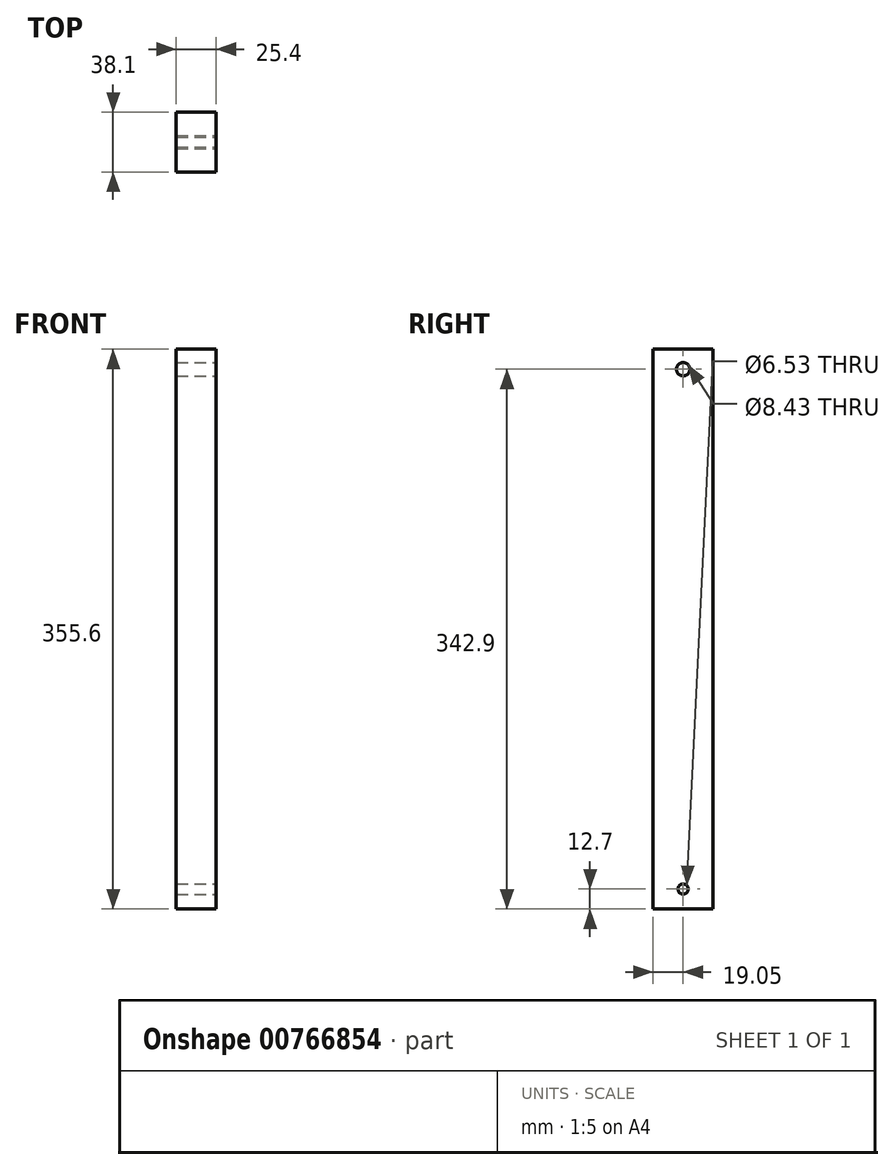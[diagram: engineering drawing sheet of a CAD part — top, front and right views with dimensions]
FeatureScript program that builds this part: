
annotation { "Feature Type Name" : "Feature", "Feature Type Description" : "" }
export const myFeature = defineFeature(function(context is Context, id is Id, definition is map)
    precondition{}
    {
        {
            var Q0;
            Q0=qCreatedBy(makeId("Right.planeOp"),FACE);
            var sketch = newSketch(context, id + "F0", { "sketchPlane" : qUnion([Q0])});
            skLineSegment(sketch, "E0.bottom", {"start": v(-19.05, 177.8) * mm, "end": v(19.05, 177.8) * mm});
            skLineSegment(sketch, "E0.top", {"start": v(-19.05, -177.8) * mm, "end": v(19.05, -177.8) * mm});
            skLineSegment(sketch, "E0.left", {"start": v(-19.05, 177.8) * mm, "end": v(-19.05, -177.8) * mm});
            skLineSegment(sketch, "E0.right", {"start": v(19.05, 177.8) * mm, "end": v(19.05, -177.8) * mm});
            skPoint(sketch, "E0.middle", {"position": v(0, 0) * mm});
            skSolve(sketch);
        }
        {
            var Q0;
            Q0=makeQuery(id+"F0.imprint","IMPRINT",FACE,{"disambiguationData":[TD([[makeQuery(id+"F0.imprint","IMPRINT",EDGE,{"derivedFrom":sQuery(id+"F0.wireOp",EDGE,"E0.bottom")}),-1.0]])]});
            extrude(context, id + "F1", {"entities" : qUnion([Q0]), "depth" : 25.4 * mm, "offsetDistance" : 25.4 * mm});
        }
        {
            var Q0;
            Q0=makeQuery(id+"F1.opExtrude","CAP_FACE",FACE,{"disambiguationData":[OSD([sQuery(id+"F0.wireOp",EDGE,"E0.bottom"),sQuery(id+"F0.wireOp",EDGE,"E0.top"),sQuery(id+"F0.wireOp",EDGE,"E0.left"),sQuery(id+"F0.wireOp",EDGE,"E0.right")])],"isStart":false});
            var sketch = newSketch(context, id + "F2", { "sketchPlane" : qUnion([Q0])});
            skLineSegment(sketch, "E1", {"start": v(0, -177.8) * mm, "end": v(0, -165.1) * mm});
            skSolve(sketch);
        }
        {
            var Q0;
            Q0=sQuery(id+"F2.wireOp",VERTEX,"E1.end");
            var Q1;
            Q1=makeQuery(id+"F1.opExtrude","SWEPT_BODY",BODY,{"disambiguationData":[OSD([sQuery(id+"F0.wireOp",EDGE,"E0.bottom"),sQuery(id+"F0.wireOp",EDGE,"E0.top"),sQuery(id+"F0.wireOp",EDGE,"E0.left"),sQuery(id+"F0.wireOp",EDGE,"E0.right")])]});
            hole(context, id + "F3", {"style" : HoleStyle.SIMPLE, "endStyle" : HoleEndStyle.THROUGH, "standardTappedOrClearance" : lookupTablePath({ "standard" : "ANSI", "engagement" : "75%", "pitch" : "18 tpi", "size" : "5/16", "type" : "Tapped" }), "standardBlindInLast" : lookupTablePath({ "standard" : "ANSI", "engagement" : "75%", "pitch" : "18 tpi", "size" : "5/16", "type" : "Tapped" }), "holeDiameter" : 6.53 * mm, "majorDiameter" : 7.94 * mm, "showTappedDepth" : true, "isTappedThrough" : true, "tappedDepth" : 12.7 * mm, "tapClearance" : 3, "startFromSketch" : true, "locations" : qUnion([Q0]), "scope" : qUnion([Q1])});
        }
        {
            var Q0;
            Q0=makeQuery(id+"F1.opExtrude","CAP_FACE",FACE,{"disambiguationData":[OSD([sQuery(id+"F0.wireOp",EDGE,"E0.bottom"),sQuery(id+"F0.wireOp",EDGE,"E0.top"),sQuery(id+"F0.wireOp",EDGE,"E0.left"),sQuery(id+"F0.wireOp",EDGE,"E0.right")])],"isStart":false});
            var sketch = newSketch(context, id + "F4", { "sketchPlane" : qUnion([Q0])});
            skLineSegment(sketch, "E2", {"start": v(0, 177.8) * mm, "end": v(0, 165.1) * mm});
            skSolve(sketch);
        }
        {
            var Q0;
            Q0=sQuery(id+"F4.wireOp",VERTEX,"E2.end");
            var Q1;
            Q1=makeQuery(id+"F1.opExtrude","SWEPT_BODY",BODY,{"disambiguationData":[OSD([sQuery(id+"F0.wireOp",EDGE,"E0.bottom"),sQuery(id+"F0.wireOp",EDGE,"E0.top"),sQuery(id+"F0.wireOp",EDGE,"E0.left"),sQuery(id+"F0.wireOp",EDGE,"E0.right")])]});
            hole(context, id + "F5", {"style" : HoleStyle.SIMPLE, "endStyle" : HoleEndStyle.THROUGH, "standardTappedOrClearance" : lookupTablePath({ "standard" : "ANSI", "fit" : "Normal (ASME)", "size" : "5/16", "type" : "Clearance" }), "standardBlindInLast" : lookupTablePath({ "fit" : "Free", "standard" : "ANSI", "size" : "5/16", "type" : "Clearance" }), "holeDiameter" : 8.43 * mm, "majorDiameter" : 7.94 * mm, "isTappedThrough" : true, "tappedDepth" : 12.7 * mm, "tapClearance" : 3, "startFromSketch" : true, "locations" : qUnion([Q0]), "scope" : qUnion([Q1])});
        }
    });
